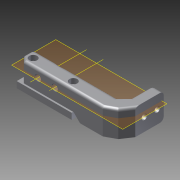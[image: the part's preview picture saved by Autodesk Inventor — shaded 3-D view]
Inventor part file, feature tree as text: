
AUTODESK INVENTOR PART (.ipt)
format: ipt  version: 2012 (Build 160160000, 160)  size: 421,376 bytes
history: native  units: mm
features: sketch x12, extrude x10, chamfer x5, fillet x4, other x2, helix x2, plane x1
ambient origin geometry x8: Origin, YZ Plane, XZ Plane, XY Plane, X Axis, Y Axis, Z Axis, Center Point
bodies: Solid1 (feature_tree)
feature tree (36):
  extrude  "Extrusion1"  Depth=12.0mm
  extrude  "Extrusion2"  Depth=21.2mm
  extrude  "Extrusion3"  Depth=22.2mm
  extrude  "Extrusion4"  Depth=22.0mm
  extrude  "Extrusion5"  Depth=5.0mm
  extrude  "Extrusion6"  Depth=5.7mm
  chamfer  "Chamfer1"  Distance=20.0mm
  chamfer  "Chamfer2"  Distance=15.0mm
  chamfer  "Chamfer3"  Distance=7.5mm
  chamfer  "Chamfer4"  Distance=10.0mm
  fillet  "Fillet1"  Radius=5.0mm
  fillet  "Fillet2"  Radius=6.0mm
  plane  "Work Plane1"
  other  "Work Axis1"
  other  "Work Axis3"
  helix  "Coil2"  [1 undecoded]
  helix  "Coil3"  [1 undecoded]
  extrude  "Extrusion9"  Depth=10.0mm TaperAngle=0.0deg
  fillet  "Fillet3"  Radius=13.0mm
  fillet  "Fillet4"  Radius=14.7mm
  extrude  "Extrusion10"  Depth=14.0mm
  chamfer  "Chamfer5"  Distance=2.0mm
  extrude  "Extrusion11"  Depth=10.0mm TaperAngle=0.0deg
  extrude  "Extrusion12"  Depth=4.2mm
  sketch  "Sketch1"  dims[d0=70.0mm d1=12.0mm d2=8.0mm]
  sketch  "Sketch2"  dims[d3=20.0mm d4=21.2mm]
  sketch  "Sketch3"  dims[d5=21.2mm d6=22.2mm]
  sketch  "Sketch4"  dims[d7=12.0mm d8=22.0mm]
  sketch  "Sketch5"  dims[d9=5.0mm d10=5.0mm]
  sketch  "Sketch6"  dims[d11=31.0mm d12=5.7mm]
  sketch  "Sketch10"  dims[d13=3.2mm]
  sketch  "Sketch12"  dims[d14=5.5mm d15=20.0mm d16=0.0mm]
  sketch  "Sketch13"  dims[d17=10.0mm]
  sketch  "Sketch14"  dims[d18=4.2mm]
  sketch  "Sketch16"  dims[d19=10.0mm]
  sketch  "Sketch17"  dims[d20=5.0mm d21=15.0mm d22=0.0mm d23=7.5mm d24=10.0mm d25=4.0mm d26=0.0mm d27=0.0mm d28=5.0mm d29=6.0mm d30=15.0mm d31=13.7mm d32=10.0mm d33=0.0mm d34=13.0mm d35=14.7mm d36=14.0mm d37=2.0mm d38=10.0mm d39=0.0mm d40=4.2mm d41=4.0mm d42=0.0mm d43=3.0mm d44=2.0mm d45=30.0deg d46=3.0mm d47=2.0mm d48=30.0deg d49=5.0mm d50=2.0mm d51=30.0deg d52=4.0mm d53=2.0mm d54=30.0deg d55=3.0mm d56=3.0mm d71=-6.0mm d80=60.0deg d81=0.75mm d82=0.0mm d86=0.8mm d87=4.2mm d88=60.0mm d89=0.0mm d90=90.0deg d91=90.0deg d92=0.0mm d93=0.0mm d94=60.0deg d95=0.75mm d96=0.0mm d97=0.8mm d98=4.2mm d99=60.0mm d100=0.0mm d101=90.0deg d102=90.0deg d103=0.0mm d104=0.0mm d105=6.0mm d106=4.0mm d107=0.0mm d108=2.0mm d109=2.0mm d110=5.0mm d111=5.0mm d112=5.0mm d113=42.4mm d114=5.0mm d115=0.0mm d116=5.0mm d117=2.0mm d118=45.0deg d119=0.5mm d121=0.25mm d122=0.5mm d123=13.0mm d124=1.0mm d125=0.0mm d126=0.0mm d127=1.5mm d128=1.5mm d129=1.5mm d130=1.5mm d131=3.5mm d132=0.0mm]
note: 2 required parameter values undecoded (feature->parameter linkage not recoverable at this tier; creation-order binding heuristic only, values carry confidence <= 0.55)
